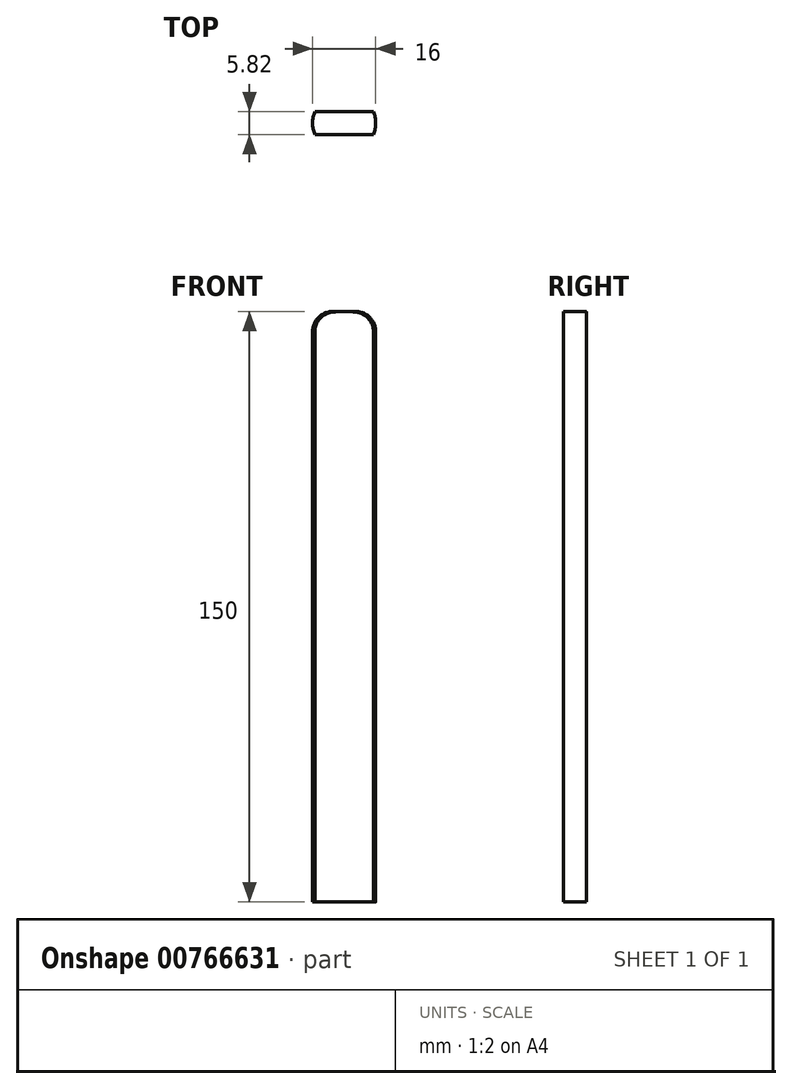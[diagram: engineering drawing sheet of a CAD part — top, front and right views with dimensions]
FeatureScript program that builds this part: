
annotation { "Feature Type Name" : "Feature", "Feature Type Description" : "" }
export const myFeature = defineFeature(function(context is Context, id is Id, definition is map)
    precondition{}
    {
        {
            var Q0;
            Q0=qCreatedBy(makeId("Top.planeOp"),FACE);
            var sketch = newSketch(context, id + "F0", { "sketchPlane" : qUnion([Q0])});
            skLineSegment(sketch, "E0.bottom", {"start": v(-7.45, 2.9) * mm, "end": v(7.45, 2.9) * mm});
            skLineSegment(sketch, "E0.top", {"start": v(-7.45, -2.9) * mm, "end": v(7.45, -2.9) * mm});
            skPoint(sketch, "E0.middle", {"position": v(0, 0) * mm});
            skArc(sketch, "E1", {"start": v(7.45, -2.9) * mm, "mid": v(8, 0) * mm, "end": v(7.45, 2.9) * mm});
            skArc(sketch, "E2.trimOffspring", {"start": v(-7.45, 2.9) * mm, "mid": v(-8, 0) * mm, "end": v(-7.45, -2.9) * mm});
            skPoint(sketch, "E3.orphan", {"position": v(-8, 2.9) * mm});
            skPoint(sketch, "E0.left.end.orphan", {"position": v(-8, -2.9) * mm});
            skPoint(sketch, "E4.orphan", {"position": v(8, -2.9) * mm});
            skPoint(sketch, "E5.orphan", {"position": v(8, 2.9) * mm});
            skSolve(sketch);
        }
        {
            var Q0;
            Q0 = qSketchRegion(id + "F0", true);
            extrude(context, id + "F1", {"entities" : qUnion([Q0]), "depth" : 150 * mm, "offsetDistance" : 25 * mm});
        }
        {
            var Q0;
            Q0=makeQuery(id+"F1.opExtrude","CAP_EDGE",EDGE,{"disambiguationData":[OSD([sQuery(id+"F0.wireOp",EDGE,"E0.right")])],"isStart":false});
            var Q1;
            Q1=makeQuery(id+"F1.opExtrude","CAP_EDGE",EDGE,{"disambiguationData":[OSD([sQuery(id+"F0.wireOp",EDGE,"E1")])],"isStart":false});
            fillet(context, id + "F2", {"entities" : qUnion([Q0, Q1]), "radius" : 5 * mm, "tangentPropagation" : true, "allowEdgeOverflow" : false});
        }
        {
            var Q0;
            Q0=makeQuery(id+"F1.opExtrude","CAP_EDGE",EDGE,{"disambiguationData":[OSD([sQuery(id+"F0.wireOp",EDGE,"E2.trimOffspring")])],"isStart":false});
            fillet(context, id + "F3", {"entities" : qUnion([Q0]), "radius" : 5 * mm, "tangentPropagation" : true, "allowEdgeOverflow" : false});
        }
    });
